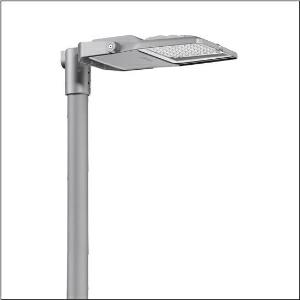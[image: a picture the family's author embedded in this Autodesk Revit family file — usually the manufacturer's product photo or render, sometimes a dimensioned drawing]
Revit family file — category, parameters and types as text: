
# Revit family: floodlight_fl_21_iq_mini___pl52_5xa7771d2d3a_64cb
name_source: partatom
category: Lighting Fixtures
units: mm (PartAtom-declared; Revit-internal decimal feet)

## family parameters
Cut with Voids When Loaded = No
Host = Face
Light Source = No
Part Type = Normal
Room Calculation Point = No
Round Connector Dimension = Use Diameter
Shared = No

## types (1)
- --- (1 x LED, 17830 lm, 143 W, 3000K)
    Apparent Load = 143 VA
    CIE Flux Codes = 26 60 98 100 100
    Color Rendering = 70
    Color Temperature = 3000K
    Default Elevation = 1800 mm
    Description = Floodlight FL 21 iQ mini, floodlight, primary light control with lens, of PMMA, primary optical cover: protective disc, of toughened safety glass, transparent, light distribution: PL52, light emission: direct distribution, installation type: surface-mounted, LED, High Power LED, rated luminous flux: 17.830lm, luminous efficacy: 125lm/W, light colour: 730, colour temperature: 3000K, control: Auto-Match, Temp-Guard, Lumen-Switch, Night-Set, Smart-Wire, Light-Fading, Desk-Remote (wireless, voltage-free reading and setting of iQ features in the workshop via application-optimized NFC function/RFID function), optimised constant luminous flux control (CLO 2.0), with terminal, 6-pole, mains connection: 220..240V, AC, 50/60Hz, start of lifetime: 143W, end of service life: 152W, reduction: 61W, luminaire housing, of diecast aluminium, powder-coated, Siteco® metallic grey (DB 702S), corrosivity category C5 mid according to DIN EN ISO 12944, sealing non-destructively replaceable, please order mast flange separately, mast bracket, of steel, galvanised, powder-coated, Siteco® metallic grey (DB 702S), protection rating (complete): IP66, insulation class (complete): insulation class II (safety insulation), certification: CE, ENEC, VDE, protection symbol: D, impact resistance: IK08, permissible operating ambient temperature: -40..+40°C, permissible operating ambient temperature for outdoor applications: -40..+50°C, standard: DIN EN 12944, LABS conformity tested according to VDMA 24364:2018-05, packaging unit: 1 piece

Light Distribution: PL52
    Height = 70 mm
    Lamp = 1 x LED
    Lamp Light Flux = 17830 lm
    Lamp Power = 143 W
    Lamp count = 1
    Length = 485 mm
    Luminous efficacy = 125 lm/W
    Manufacturer = Siteco
    ModVariant = No
    Model = 5XA7771D2D3A
    Number of Poles = 1
    OnlyDefault = Yes
    Power Factor = 1
    Product Name = Floodlight FL 21 iQ mini | PL52
    Product group = floodlight | pylon annexe
    ProductGroupID = 6200
    Protection Class = Protection class II
    Protection Degree = IP 66
    RLX_Detail_Level = 1
    RLX_Emergency_Light_Flux = 0 lm
    RLX_Emergency_Type = 0
    RLX_Emergency_Type_DB = No
    RlxData = <blob elided: 101805 chars, md5=3eaf56e6>
    Socket = socket
    Standby Power = 0 W
    System Light Flux = 17830 lm
    System Power = 143 W
    Type Comments = factory setting: luminous flux: 100 % | dim-lin: 254 | 730 mA
    Type Image = l_1007125.jpg
    URL = http://relux.com
    VarID = @adj_134311
    Voltage = 0 V
    Weight = 0.00 kg
    Width = 337 mm

## geometry (parser evidence)
native form markers: Blend x4, Sweep x11
no freeform markers — native parametric forms only
